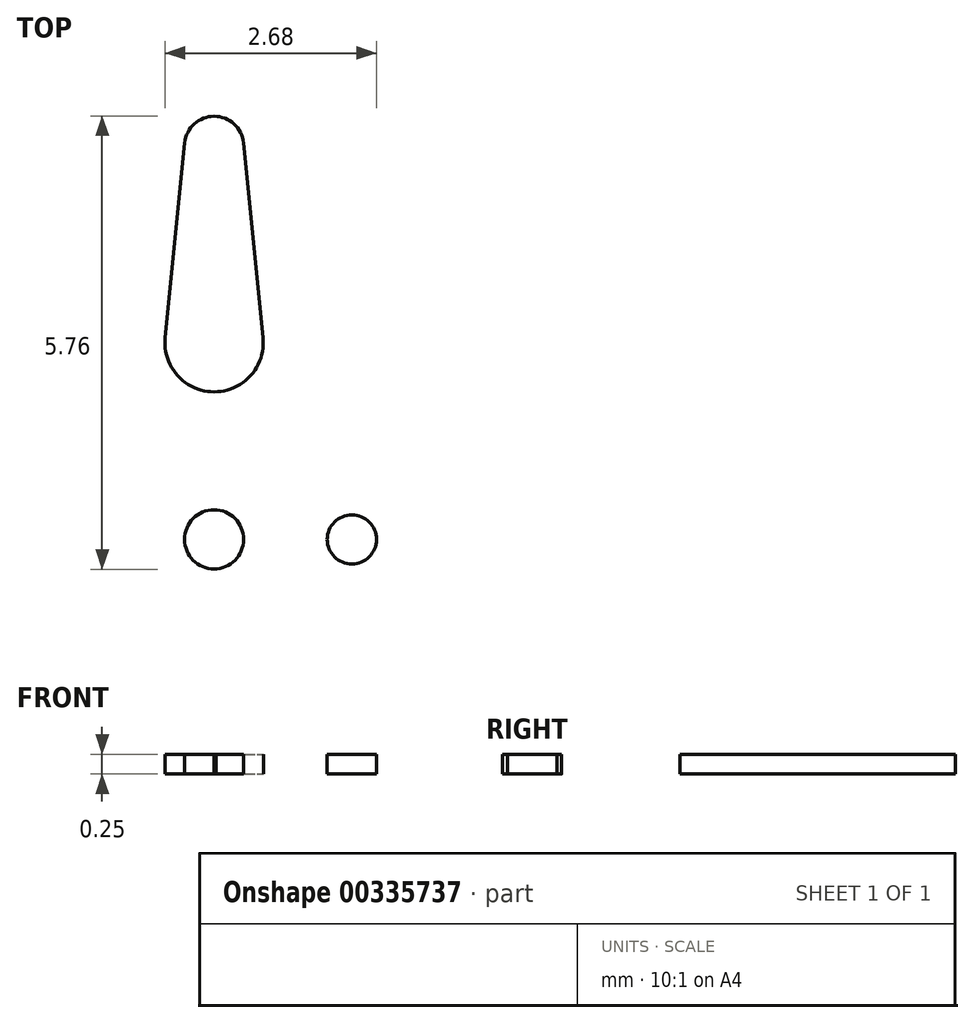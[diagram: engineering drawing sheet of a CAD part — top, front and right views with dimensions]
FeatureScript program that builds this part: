
annotation { "Feature Type Name" : "Feature", "Feature Type Description" : "" }
export const myFeature = defineFeature(function(context is Context, id is Id, definition is map)
    precondition{}
    {
        {
            var Q0;
            Q0=qCreatedBy(makeId("Top.planeOp"),FACE);
            var sketch = newSketch(context, id + "F0", { "sketchPlane" : qUnion([Q0])});
            skLineSegment(sketch, "E0", {"start": v(0, 0) * mm, "end": v(0, 5) * mm, "construction": true});
            skCircle(sketch, "E1", {"center": v(0, 0) * mm, "radius": 0.38 * mm});
            skCircle(sketch, "E2", {"center": v(0, 2.5) * mm, "radius": 0.62 * mm});
            skCircle(sketch, "E3", {"center": v(0, 5) * mm, "radius": 0.38 * mm});
            skLineSegment(sketch, "E4", {"start": v(0, 0) * mm, "end": v(1.75, 0) * mm, "construction": true});
            skCircle(sketch, "E5", {"center": v(1.75, 0) * mm, "radius": 0.31 * mm});
            skLineSegment(sketch, "E6", {"start": v(-0.37, 5.04) * mm, "end": v(-0.62, 2.56) * mm});
            skLineSegment(sketch, "E7", {"start": v(-0.62, 2.44) * mm, "end": v(-0.38, 0) * mm});
            skLineSegment(sketch, "E8", {"start": v(0.37, 5.04) * mm, "end": v(0.62, 2.56) * mm});
            skLineSegment(sketch, "E9", {"start": v(0, -0.38) * mm, "end": v(1.76, -0.31) * mm});
            skLineSegment(sketch, "E10", {"start": v(0.62, 2.44) * mm, "end": v(0.45, 0.68) * mm});
            skLineSegment(sketch, "E11", {"start": v(0.73, 0.35) * mm, "end": v(1.76, 0.31) * mm});
            skArc(sketch, "E12.filletArc", {"start": v(0.45, 0.68) * mm, "mid": v(0.52, 0.45) * mm, "end": v(0.73, 0.35) * mm});
            skSolve(sketch);
        }
        {
            var Q0;
            {var subQ0=sQuery(id+"F0.wireOp",EDGE,"E6");Q0=makeQuery(id+"F0.imprint","IMPRINT",FACE,{"disambiguationData":[TD([[makeQuery(id+"F0.imprint","IMPRINT",EDGE,{"derivedFrom":subQ0}),1.0]])]});}
            var Q1;
            {var subQ0=sQuery(id+"F0.wireOp",EDGE,"E3");var subQ1=makeQuery(id+"F0.imprint","INTERSECT",VERTEX,{"derivedFrom":[subQ0,sQuery(id+"F0.wireOp",EDGE,"E6")]});Q1=makeQuery(id+"F0.imprint","IMPRINT",FACE,{"disambiguationData":[TD([[makeQuery(id+"F0.imprint","IMPRINT",EDGE,{"disambiguationData":[TD([[subQ1,1.0]])],"derivedFrom":subQ0}),1.0]])]});}
            var Q2;
            {var subQ0=sQuery(id+"F0.wireOp",EDGE,"E2");var subQ3=makeQuery(id+"F0.imprint","IMPRINT",VERTEX,{"disambiguationData":[OD(0.0)],"derivedFrom":subQ0});Q2=makeQuery(id+"F0.imprint","IMPRINT",FACE,{"disambiguationData":[TD([[makeQuery(id+"F0.imprint","IMPRINT",EDGE,{"disambiguationData":[TD([[subQ3,-1.0]])],"derivedFrom":subQ0}),1.0]])]});}
            var Q3;
            {var subQ0=sQuery(id+"F0.wireOp",EDGE,"E9");var subQ1=sQuery(id+"F0.wireOp",EDGE,"E1");var subQ2=makeQuery(id+"F0.imprint","INTERSECT",VERTEX,{"disambiguationData":[OD(0.0)],"derivedFrom":[subQ1,subQ0]});Q3=makeQuery(id+"F0.imprint","IMPRINT",FACE,{"disambiguationData":[TD([[makeQuery(id+"F0.imprint","IMPRINT",EDGE,{"disambiguationData":[TD([[subQ2,1.0]])],"derivedFrom":subQ1}),1.0]])]});}
            var Q4;
            {var subQ0=sQuery(id+"F0.wireOp",EDGE,"E5");var subQ1=makeQuery(id+"F0.imprint","IMPRINT",VERTEX,{"disambiguationData":[OD(0.0)],"derivedFrom":subQ0});Q4=makeQuery(id+"F0.imprint","IMPRINT",FACE,{"disambiguationData":[TD([[makeQuery(id+"F0.imprint","IMPRINT",EDGE,{"disambiguationData":[TD([[subQ1,1.0]])],"derivedFrom":subQ0}),1.0]])]});}
            extrude(context, id + "F1", {"entities" : qUnion([Q0, Q1, Q2, Q3, Q4]), "depth" : 0.25 * mm});
        }
        {
            var Q0;
            Q0 = qSketchRegion(id + "F0", true);
            extrude(context, id + "F2", {"entities" : qUnion([Q0]), "depth" : 0.25 * mm});
        }
    });
